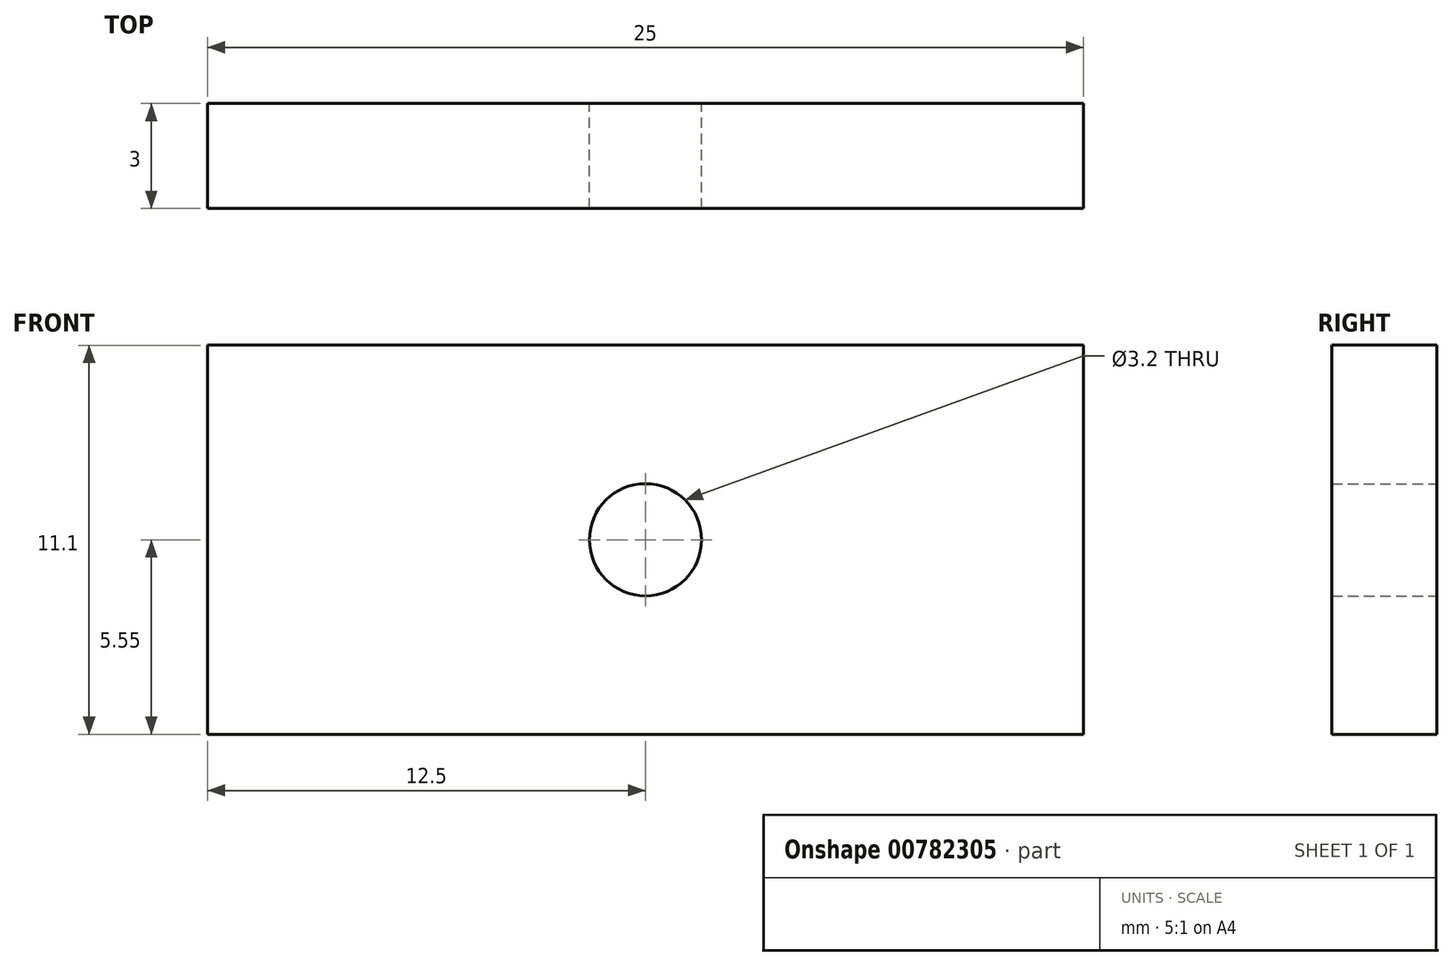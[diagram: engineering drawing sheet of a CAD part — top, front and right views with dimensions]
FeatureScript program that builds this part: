
annotation { "Feature Type Name" : "Feature", "Feature Type Description" : "" }
export const myFeature = defineFeature(function(context is Context, id is Id, definition is map)
    precondition{}
    {
        {
            var Q0;
            Q0=qCreatedBy(makeId("Front.planeOp"),FACE);
            var sketch = newSketch(context, id + "F0", { "sketchPlane" : qUnion([Q0])});
            skLineSegment(sketch, "E0.bottom", {"start": v(-12.5, -5.55) * mm, "end": v(12.5, -5.55) * mm});
            skLineSegment(sketch, "E0.top", {"start": v(-12.5, 5.56) * mm, "end": v(12.5, 5.56) * mm});
            skLineSegment(sketch, "E0.left", {"start": v(-12.5, -5.55) * mm, "end": v(-12.5, 5.56) * mm});
            skLineSegment(sketch, "E0.right", {"start": v(12.5, -5.55) * mm, "end": v(12.5, 5.56) * mm});
            skPoint(sketch, "E0.middle", {"position": v(0, 0) * mm});
            skCircle(sketch, "E1", {"center": v(0, 0) * mm, "radius": 1.6 * mm});
            skSolve(sketch);
        }
        {
            var Q0;
            Q0=makeQuery(id+"F0.imprint","IMPRINT",FACE,{"disambiguationData":[TD([[makeQuery(id+"F0.imprint","IMPRINT",EDGE,{"derivedFrom":sQuery(id+"F0.wireOp",EDGE,"E0.bottom")}),1.0]])]});
            extrude(context, id + "F1", {"entities" : qUnion([Q0]), "depth" : 3 * mm, "offsetDistance" : 25 * mm});
        }
    });
